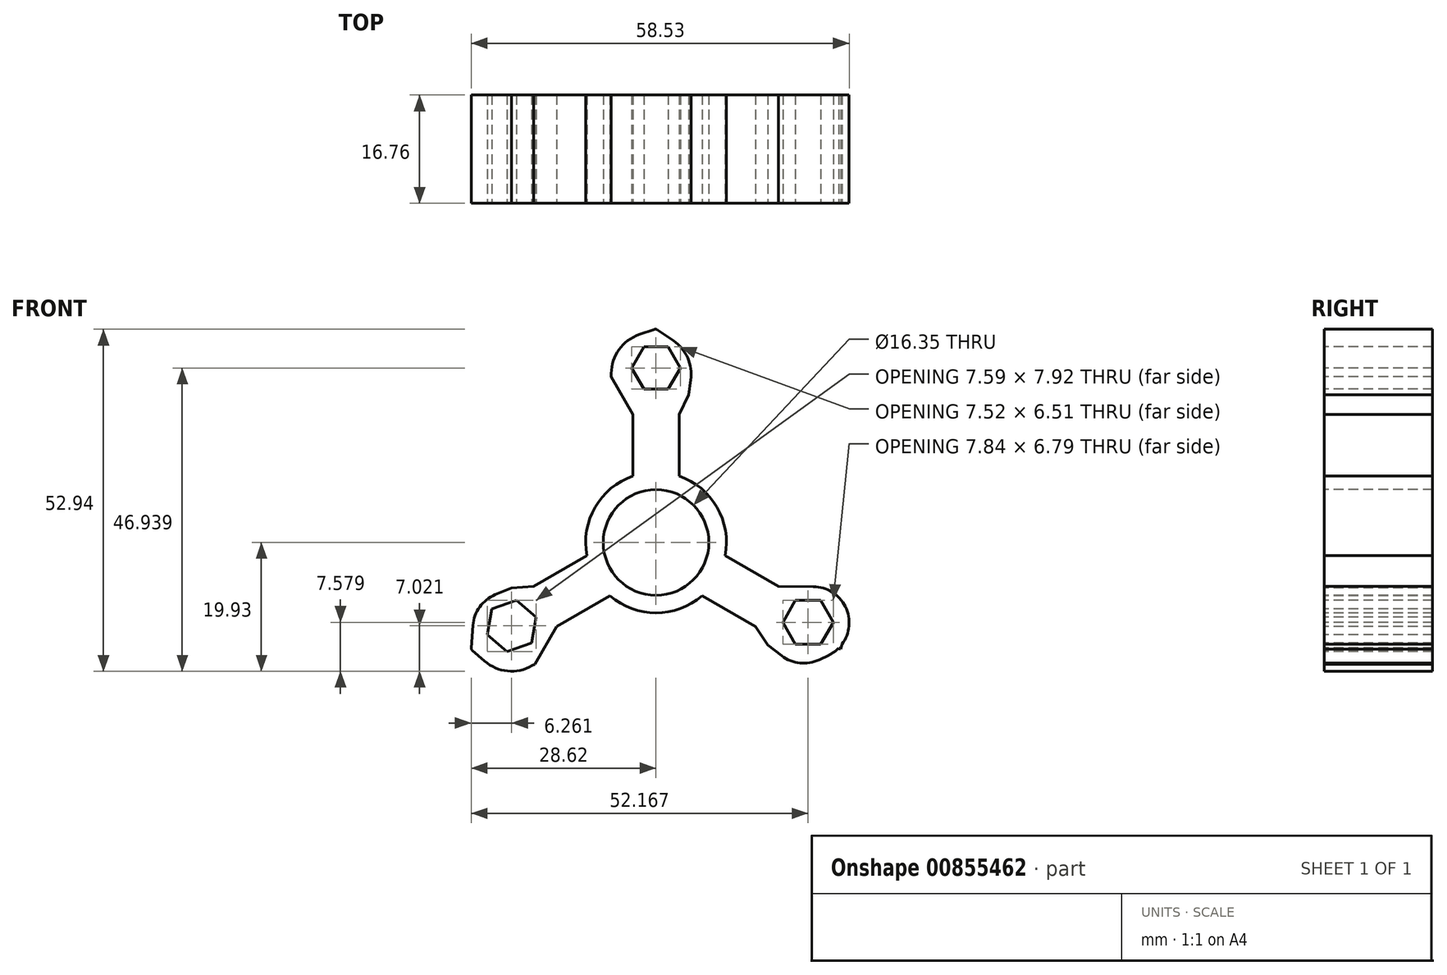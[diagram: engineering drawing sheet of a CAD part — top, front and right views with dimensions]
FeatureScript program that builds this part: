
annotation { "Feature Type Name" : "Feature", "Feature Type Description" : "" }
export const myFeature = defineFeature(function(context is Context, id is Id, definition is map)
    precondition{}
    {
        {
            var Q0;
            Q0=qCreatedBy(makeId("Front.planeOp"),FACE);
            var sketch = newSketch(context, id + "F0", { "sketchPlane" : qUnion([Q0])});
            skCircle(sketch, "E0", {"center": v(0, 0) * mm, "radius": 10.9 * mm});
            skLineSegment(sketch, "E1", {"start": v(-0.27, 32.97) * mm, "end": v(-2.63, 32.17) * mm});
            skLineSegment(sketch, "E2", {"start": v(-6.92, 26.16) * mm, "end": v(-6.92, 25.68) * mm});
            skLineSegment(sketch, "E3", {"start": v(2.68, 31.24) * mm, "end": v(0.24, 32.9) * mm});
            skLineSegment(sketch, "E4.1.2", {"start": v(-28.36, -12.83) * mm, "end": v(-28.62, -16.31) * mm});
            skLineSegment(sketch, "E4.1.4", {"start": v(-19.2, -19.08) * mm, "end": v(-18.78, -18.83) * mm});
            skLineSegment(sketch, "E4.1.6", {"start": v(-28.47, -16.68) * mm, "end": v(-26.55, -18.36) * mm});
            skLineSegment(sketch, "E4.2.2", {"start": v(25.29, -18.14) * mm, "end": v(26.74, -17.44) * mm});
            skLineSegment(sketch, "E4.2.4", {"start": v(26.6, -7.36) * mm, "end": v(25.87, -6.95) * mm});
            skLineSegment(sketch, "E4.2.6", {"start": v(28.64, -16.53) * mm, "end": v(29.28, -13.27) * mm});
            skCircle(sketch, "E5.cCircle", {"center": v(0, 27) * mm, "radius": 3.26 * mm, "construction": true});
            skLineSegment(sketch, "E5.0", {"start": v(1.88, 23.75) * mm, "end": v(-1.88, 23.75) * mm});
            skLineSegment(sketch, "E5.1", {"start": v(-1.88, 23.75) * mm, "end": v(-3.76, 27) * mm});
            skLineSegment(sketch, "E5.2", {"start": v(-3.76, 27) * mm, "end": v(-1.88, 30.27) * mm});
            skLineSegment(sketch, "E5.3", {"start": v(-1.88, 30.27) * mm, "end": v(1.88, 30.27) * mm});
            skLineSegment(sketch, "E5.4", {"start": v(1.88, 30.27) * mm, "end": v(3.76, 27) * mm});
            skLineSegment(sketch, "E5.5", {"start": v(3.76, 27) * mm, "end": v(1.88, 23.75) * mm});
            skPoint(sketch, "E5.0.midPoint", {"position": v(0, 23.75) * mm});
            skCircle(sketch, "E6.cCircle", {"center": v(23.55, -12.35) * mm, "radius": 3.4 * mm, "construction": true});
            skLineSegment(sketch, "E6.0", {"start": v(25.5, -15.74) * mm, "end": v(21.59, -15.74) * mm});
            skLineSegment(sketch, "E6.1", {"start": v(21.59, -15.74) * mm, "end": v(19.63, -12.35) * mm});
            skLineSegment(sketch, "E6.2", {"start": v(19.63, -12.35) * mm, "end": v(21.59, -8.96) * mm});
            skLineSegment(sketch, "E6.3", {"start": v(21.59, -8.96) * mm, "end": v(25.5, -8.96) * mm});
            skLineSegment(sketch, "E6.4", {"start": v(25.5, -8.96) * mm, "end": v(27.47, -12.35) * mm});
            skLineSegment(sketch, "E6.5", {"start": v(27.47, -12.35) * mm, "end": v(25.5, -15.74) * mm});
            skPoint(sketch, "E6.0.midPoint", {"position": v(23.55, -15.74) * mm});
            skCircle(sketch, "E7.cCircle", {"center": v(-22.36, -12.9) * mm, "radius": 3.49 * mm, "construction": true});
            skLineSegment(sketch, "E7.0", {"start": v(-18.56, -11.56) * mm, "end": v(-19.3, -15.52) * mm});
            skLineSegment(sketch, "E7.1", {"start": v(-19.3, -15.52) * mm, "end": v(-23.1, -16.87) * mm});
            skLineSegment(sketch, "E7.2", {"start": v(-23.1, -16.87) * mm, "end": v(-26.15, -14.26) * mm});
            skLineSegment(sketch, "E7.3", {"start": v(-26.15, -14.26) * mm, "end": v(-25.42, -10.3) * mm});
            skLineSegment(sketch, "E7.4", {"start": v(-25.42, -10.3) * mm, "end": v(-21.63, -8.95) * mm});
            skLineSegment(sketch, "E7.5", {"start": v(-21.63, -8.95) * mm, "end": v(-18.56, -11.56) * mm});
            skPoint(sketch, "E7.0.midPoint", {"position": v(-18.93, -13.54) * mm});
            skLineSegment(sketch, "E8.trimOffspring", {"start": v(20.07, -11.59) * mm, "end": v(20.22, -11.68) * mm});
            skLineSegment(sketch, "E9.trimOffspring", {"start": v(-18.26, -10.54) * mm, "end": v(-19.34, -11.17) * mm});
            skLineSegment(sketch, "E10.trimOffspring", {"start": v(0, 21.08) * mm, "end": v(0, 33.07) * mm});
            skPoint(sketch, "E11.0.internal.orphan", {"position": v(-9.44, -5.45) * mm});
            skPoint(sketch, "E11.1.internal.orphan", {"position": v(-9.44, -10.34) * mm});
            skLineSegment(sketch, "E12", {"start": v(-3.57, 19.82) * mm, "end": v(-3.57, 10.3) * mm});
            skLineSegment(sketch, "E13.MirrorCS", {"start": v(3.57, 19.82) * mm, "end": v(3.57, 10.3) * mm});
            skLineSegment(sketch, "E14.MirrorCS", {"start": v(15.37, -13) * mm, "end": v(7.13, -8.24) * mm});
            skLineSegment(sketch, "E15.MirrorCS", {"start": v(18.95, -6.81) * mm, "end": v(10.7, -2.05) * mm});
            skLineSegment(sketch, "E16.MirrorCS", {"start": v(-18.95, -6.81) * mm, "end": v(-10.7, -2.05) * mm});
            skLineSegment(sketch, "E17.MirrorCS", {"start": v(-15.37, -13) * mm, "end": v(-7.13, -8.24) * mm});
            skLineSegment(sketch, "E18", {"start": v(5.08, 22.89) * mm, "end": v(3.57, 19.82) * mm});
            skLineSegment(sketch, "E19", {"start": v(17.28, -15.84) * mm, "end": v(15.37, -13) * mm});
            skLineSegment(sketch, "E20", {"start": v(-18.95, -6.81) * mm, "end": v(-22.36, -7.04) * mm});
            skCircle(sketch, "E21", {"center": v(0, 0) * mm, "radius": 8.18 * mm});
            skLineSegment(sketch, "E22", {"start": v(5.08, 22.89) * mm, "end": v(5.39, 25.14) * mm});
            skLineSegment(sketch, "E23", {"start": v(-6.92, 25.68) * mm, "end": v(-3.57, 19.82) * mm});
            skLineSegment(sketch, "E24", {"start": v(-22.36, -7.04) * mm, "end": v(-24.9, -8.09) * mm});
            skLineSegment(sketch, "E25", {"start": v(-18.78, -18.83) * mm, "end": v(-15.37, -13) * mm});
            skLineSegment(sketch, "E26", {"start": v(17.28, -15.84) * mm, "end": v(19.45, -17.53) * mm});
            skLineSegment(sketch, "E27", {"start": v(24.35, -6.84) * mm, "end": v(18.95, -6.81) * mm});
            skPoint(sketch, "E28.visualSharp", {"position": v(-6.92, 30.7) * mm});
            skArc(sketch, "E28.filletArc", {"start": v(-2.63, 32.17) * mm, "mid": v(-5.74, 29.85) * mm, "end": v(-6.92, 26.16) * mm});
            skPoint(sketch, "E29.visualSharp", {"position": v(5.92, 29.03) * mm});
            skArc(sketch, "E29.filletArc", {"start": v(5.39, 25.14) * mm, "mid": v(4.9, 28.57) * mm, "end": v(2.68, 31.24) * mm});
            skPoint(sketch, "E30.visualSharp", {"position": v(0, 33.07) * mm});
            skArc(sketch, "E30.filletArc", {"start": v(0.24, 32.9) * mm, "mid": v(0, 33) * mm, "end": v(-0.27, 32.97) * mm});
            skPoint(sketch, "E31.visualSharp", {"position": v(-28.1, -9.39) * mm});
            skArc(sketch, "E31.filletArc", {"start": v(-27.76, -9.25) * mm, "mid": v(-28.01, -9.45) * mm, "end": v(-28.12, -9.75) * mm});
            skPoint(sketch, "E32.visualSharp", {"position": v(-23.13, -21.34) * mm});
            skArc(sketch, "E32.filletArc", {"start": v(-23.44, -21.07) * mm, "mid": v(-23.11, -21.21) * mm, "end": v(-22.77, -21.14) * mm});
            skArc(sketch, "E33.filletArc", {"start": v(-26.55, -18.36) * mm, "mid": v(-22.99, -19.9) * mm, "end": v(-19.2, -19.08) * mm});
            skPoint(sketch, "E34.visualSharp", {"position": v(-28.64, -16.53) * mm});
            skArc(sketch, "E34.filletArc", {"start": v(-28.62, -16.31) * mm, "mid": v(-28.59, -16.51) * mm, "end": v(-28.47, -16.68) * mm});
            skArc(sketch, "E35.filletArc", {"start": v(-27.65, -9.2) * mm, "mid": v(-27.99, -9.47) * mm, "end": v(-28.13, -9.86) * mm});
            skPoint(sketch, "E36.visualSharp", {"position": v(25.7, -6.84) * mm});
            skArc(sketch, "E36.filletArc", {"start": v(25.87, -6.95) * mm, "mid": v(25.7, -6.87) * mm, "end": v(25.5, -6.84) * mm});
            skPoint(sketch, "E37.newPointA", {"position": v(28.64, -16.53) * mm});
            skArc(sketch, "E37.filletArc", {"start": v(26.74, -17.44) * mm, "mid": v(29.77, -11.19) * mm, "end": v(24.35, -6.84) * mm});
            skPoint(sketch, "E38.visualSharp", {"position": v(22.18, -19.64) * mm});
            skArc(sketch, "E38.filletArc", {"start": v(19.45, -17.53) * mm, "mid": v(22.28, -18.66) * mm, "end": v(25.29, -18.14) * mm});
            skPoint(sketch, "E39.visualSharp", {"position": v(30.05, -9.36) * mm});
            skArc(sketch, "E39.filletArc", {"start": v(29.28, -13.27) * mm, "mid": v(28.88, -9.88) * mm, "end": v(26.6, -7.36) * mm});
            skArc(sketch, "E40.filletArc", {"start": v(-24.9, -8.09) * mm, "mid": v(-27.3, -9.97) * mm, "end": v(-28.36, -12.83) * mm});
            skLineSegment(sketch, "E41.trimOffspring", {"start": v(25.8, -14.9) * mm, "end": v(25.95, -14.98) * mm});
            skLineSegment(sketch, "E42.trimOffspring", {"start": v(28.3, -16.34) * mm, "end": v(28.64, -16.53) * mm});
            skLineSegment(sketch, "E43.trimOffspring", {"start": v(-28.6, -16.5) * mm, "end": v(-28.64, -16.53) * mm});
            skLineSegment(sketch, "E44.trimOffspring", {"start": v(-25.38, -14.65) * mm, "end": v(-25.56, -14.76) * mm});
            skSolve(sketch);
        }
        {
            var Q0;
            Q0 = qSketchRegion(id + "F0", true);
            extrude(context, id + "F1", {"entities" : qUnion([Q0]), "oppositeDirection" : true, "depth" : 16.76 * mm, "offsetDistance" : 25.4 * mm});
        }
    });
